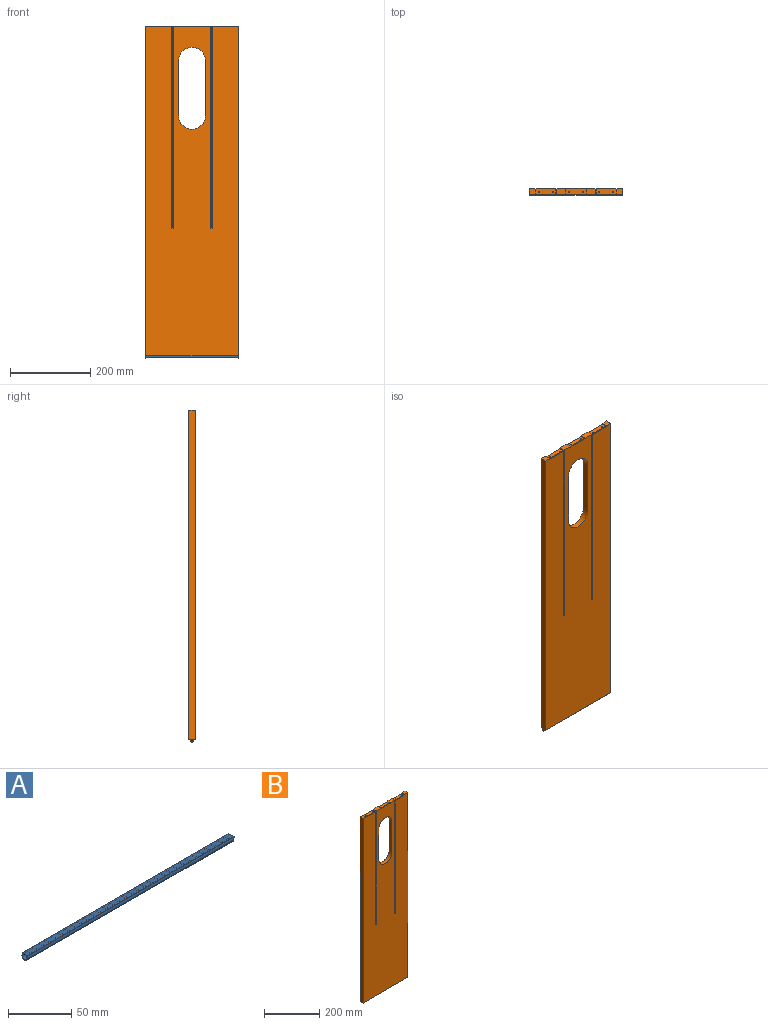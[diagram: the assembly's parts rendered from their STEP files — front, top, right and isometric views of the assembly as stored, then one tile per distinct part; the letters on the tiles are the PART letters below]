
ASSEMBLY  parts=2 mates=1
PART A: 10 faces, bbox 230x6.2x5.8 mm
  f0: plane 230x6mm, normal (0,0,1), area 1380mm2, adj f1,f7,f8,f9
  f1: plane 230x0.5mm, normal (0,-1,0), area 115mm2, adj f0,f2,f8,f9
  f2: plane 230x1.2mm, normal (0,0,-1), area 275.7mm2, adj f1,f3,f8,f9
  f3: cylinder r=3mm len=230mm, axis (1,0,0), area 3349.7mm2, adj f2,f4,f8,f9
  f4: plane 230x0.87mm, normal (0,0,-1), area 200.3mm2, adj f3,f7,f8,f9
  f5: cylinder r=2.5mm len=230mm, axis (1,0,0), area 3112.1mm2, adj f6,f8,f9
  f6: plane 230x2.11mm, normal (0,0,-1), area 485.1mm2, adj f5,f8,f9
  f7: plane 230x0.5mm, normal (0,1,0), area 115mm2, adj f0,f4,f8,f9
  f8: plane 6.16x5.77mm, normal (-1,0,0), area 10mm2, adj f0,f1,f2,f3,f4,f5,f6,f7
  f9: plane 6.16x5.77mm, normal (1,0,0), area 10mm2, adj f0,f1,f2,f3,f4,f5,f6,f7
PART B: 48 faces, bbox 230x15x820 mm
  f0: plane 503x15mm, normal (-1,0,0), area 7506.5mm2, adj f2,f4,f6,f11,f26,f27
  f1: plane 503x15mm, normal (1,0,0), area 7506.5mm2, adj f2,f3,f4,f13,f22,f24
  f2: plane 820x230mm, normal (0,1,0), area 172442.8mm2, adj f0,f1,f3,f5,f6,f7,f8,f9
  f3: plane 65x15mm, normal (0,0,1), area 273mm2, adj f1,f2,f4,f8,f23,f24,f47
  f4: plane 820x230mm, normal (0,-1,0), area 172877.3mm2, adj f0,f1,f3,f5,f6,f7,f8,f9
  f5: plane 96x15mm, normal (0,0,1), area 734mm2, adj f2,f4,f10,f12,f14,f15,f16,f17
  f6: plane 65x15mm, normal (0,0,1), area 273mm2, adj f0,f2,f4,f9,f25,f27,f44
  f7: plane 230x15mm, normal (0,0,-1), area 3450mm2, adj f2,f4,f8,f9
  f8: plane 820x15mm, normal (-1,0,0), area 12300mm2, adj f2,f3,f4,f7
  f9: plane 820x15mm, normal (1,0,0), area 12300mm2, adj f2,f4,f6,f7
  f10: plane 503x13mm, normal (1,0,0), area 6539mm2, adj f5,f11,f15,f16
  f11: plane 15x3mm, normal (0,0,1), area 31mm2, adj f0,f2,f4,f10,f15,f16
  f12: plane 503x13mm, normal (-1,0,0), area 6539mm2, adj f5,f13,f14,f17
  f13: plane 15x3mm, normal (0,0,1), area 31mm2, adj f1,f2,f4,f12,f14,f17
  f14: plane 503x1mm, normal (-0.71,0.71,0), area 711.3mm2, adj f2,f5,f12,f13
  f15: plane 503x1mm, normal (0.71,0.71,0), area 711.3mm2, adj f2,f5,f10,f11
  f16: plane 503x1mm, normal (0.71,-0.71,0), area 711.3mm2, adj f4,f5,f10,f11
  f17: plane 503x1mm, normal (-0.71,-0.71,0), area 711.3mm2, adj f4,f5,f12,f13
  f18: cylinder r=33.5mm len=67mm, axis (0,-1,0), area 1578.7mm2, adj f2,f4,f19,f21
  f19: plane 137x15mm, normal (1,0,0), area 2055mm2, adj f2,f4,f18,f20
  f20: cylinder r=33.5mm len=67mm, axis (0,-1,0), area 1578.7mm2, adj f2,f4,f19,f21
  f21: plane 137x15mm, normal (-1,0,0), area 2055mm2, adj f2,f4,f18,f20
  f22: plane 52x14mm, normal (0,0,1), area 695.7mm2, adj f1,f2,f23,f24,f40,f42,f47
  f23: plane 12x2.75mm, normal (1,0,0), area 33mm2, adj f3,f22,f24,f47
  f24: plane 50x2.75mm, normal (0,1,0), area 137.5mm2, adj f1,f3,f22,f23
  f25: plane 12x2.75mm, normal (-1,0,0), area 33mm2, adj f6,f26,f27,f44
  f26: plane 52x14mm, normal (0,0,1), area 695.7mm2, adj f0,f2,f25,f27,f36,f38,f44
  f27: plane 50x2.75mm, normal (0,1,0), area 137.5mm2, adj f0,f6,f25,f26
  f28: plane 12x2.75mm, normal (-1,0,0), area 33mm2, adj f5,f29,f31,f45
  f29: plane 54x14mm, normal (0,0,1), area 697.7mm2, adj f2,f28,f30,f31,f32,f34,f45,f46
  f30: plane 12x2.75mm, normal (1,0,0), area 33mm2, adj f5,f29,f31,f46
  f31: plane 50x2.75mm, normal (0,1,0), area 137.5mm2, adj f5,f28,f29,f30
  f32: cylinder r=1mm len=12.25mm, axis (0,0,1), area 77mm2, adj f29,f33
  f33: cone r=0mm half-angle=59deg, axis (0,0,1), area 3.7mm2, adj f32
  f34: cylinder r=1mm len=12.25mm, axis (0,0,1), area 77mm2, adj f29,f35
  f35: cone r=0mm half-angle=59deg, axis (0,0,1), area 3.7mm2, adj f34
  f36: cylinder r=1mm len=12.25mm, axis (0,0,1), area 77mm2, adj f26,f37
  f37: cone r=0mm half-angle=59deg, axis (0,0,1), area 3.7mm2, adj f36
  f38: cylinder r=1mm len=12.25mm, axis (0,0,1), area 77mm2, adj f26,f39
  f39: cone r=0mm half-angle=59deg, axis (0,0,1), area 3.7mm2, adj f38
  f40: cylinder r=1mm len=12.25mm, axis (0,0,1), area 77mm2, adj f22,f41
  f41: cone r=0mm half-angle=59deg, axis (0,0,1), area 3.7mm2, adj f40
  f42: cylinder r=1mm len=12.25mm, axis (0,0,1), area 77mm2, adj f22,f43
  f43: cone r=0mm half-angle=59deg, axis (0,0,1), area 3.7mm2, adj f42
  f44: plane 2.75x2mm, normal (-0.71,0.71,0), area 7.8mm2, adj f2,f6,f25,f26
  f45: plane 2.75x2mm, normal (-0.71,0.71,0), area 7.8mm2, adj f2,f5,f28,f29
  f46: plane 2.75x2mm, normal (0.71,0.71,0), area 7.8mm2, adj f2,f5,f29,f30
  f47: plane 2.75x2mm, normal (0.71,0.71,0), area 7.8mm2, adj f2,f3,f22,f23
PLACE A t=(0,0.16,0)mm
PLACE B at identity fixed
MATE fastened A.f0 <-> B.f7  axis (0,0,1) through (0,7.5,-820)mm
